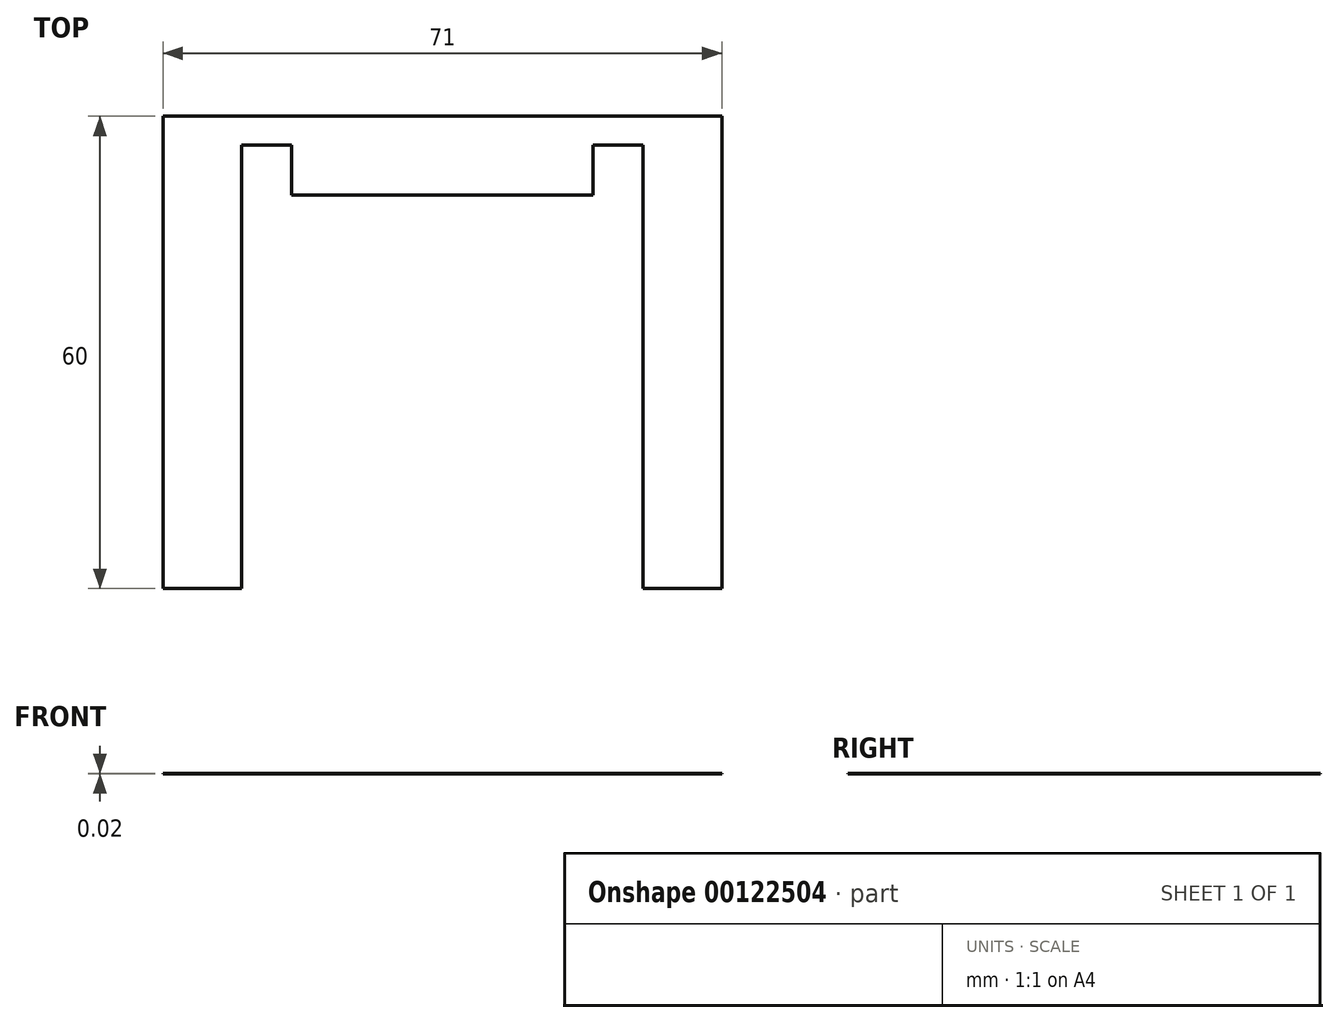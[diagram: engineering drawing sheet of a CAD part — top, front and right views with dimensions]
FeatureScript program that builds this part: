
annotation { "Feature Type Name" : "Feature", "Feature Type Description" : "" }
export const myFeature = defineFeature(function(context is Context, id is Id, definition is map)
    precondition{}
    {
        {
            var Q0;
            Q0=qCreatedBy(makeId("Top.planeOp"),FACE);
            var sketch = newSketch(context, id + "F0", { "sketchPlane" : qUnion([Q0])});
            skLineSegment(sketch, "E0.bottom", {"start": v(0, 0) * mm, "end": v(71, 0) * mm});
            skLineSegment(sketch, "E0.top", {"start": v(0, 60) * mm, "end": v(71, 60) * mm});
            skLineSegment(sketch, "E0.left", {"start": v(0, 0) * mm, "end": v(0, 60) * mm});
            skLineSegment(sketch, "E0.right", {"start": v(71, 0) * mm, "end": v(71, 60) * mm});
            skLineSegment(sketch, "E1", {"start": v(35.5, 60) * mm, "end": v(35.5, 0) * mm, "construction": true});
            skLineSegment(sketch, "E2", {"start": v(19.5, 43) * mm, "end": v(51.5, 43) * mm, "construction": true});
            skPoint(sketch, "E3", {"position": v(35.5, 43) * mm});
            skPoint(sketch, "E4", {"position": v(35.5, 50) * mm});
            skLineSegment(sketch, "E5", {"start": v(10, 50) * mm, "end": v(10, 0) * mm});
            skLineSegment(sketch, "E6", {"start": v(61, 50) * mm, "end": v(61, 0) * mm});
            skCircle(sketch, "E7", {"center": v(19.5, 43) * mm, "radius": 2.5 * mm});
            skCircle(sketch, "E8", {"center": v(51.5, 43) * mm, "radius": 2.5 * mm});
            skLineSegment(sketch, "E9", {"start": v(10, 50) * mm, "end": v(10, 56.35) * mm});
            skLineSegment(sketch, "E10", {"start": v(10, 56.35) * mm, "end": v(16.35, 56.35) * mm});
            skLineSegment(sketch, "E11", {"start": v(16.35, 56.35) * mm, "end": v(16.35, 50) * mm});
            skLineSegment(sketch, "E12.MirrorCS", {"start": v(54.65, 56.35) * mm, "end": v(54.65, 50) * mm});
            skLineSegment(sketch, "E13.MirrorCS", {"start": v(54.65, 50) * mm, "end": v(16.35, 50) * mm});
            skLineSegment(sketch, "E14.MirrorCS", {"start": v(61, 50) * mm, "end": v(61, 56.35) * mm});
            skLineSegment(sketch, "E15.MirrorCS", {"start": v(61, 56.35) * mm, "end": v(54.65, 56.35) * mm});
            skLineSegment(sketch, "E16", {"start": v(16.35, 50) * mm, "end": v(10, 50) * mm, "construction": true});
            skLineSegment(sketch, "E17", {"start": v(61, 50) * mm, "end": v(54.65, 50) * mm, "construction": true});
            skLineSegment(sketch, "E18", {"start": v(16.35, 56.35) * mm, "end": v(54.65, 56.35) * mm, "construction": true});
            skSolve(sketch);
        }
        {
            var Q0;
            {var subQ5=sQuery(id+"F0.wireOp",EDGE,"E0.left");Q0=makeQuery(id+"F0.imprint","IMPRINT",FACE,{"disambiguationData":[TD([[makeQuery(id+"F0.imprint","IMPRINT",EDGE,{"derivedFrom":subQ5}),-1.0]])]});}
            var Q1;
            {var subQ0=sQuery(id+"F0.wireOp",EDGE,"E5");Q1=makeQuery(id+"F0.imprint","IMPRINT",FACE,{"disambiguationData":[TD([[makeQuery(id+"F0.imprint","IMPRINT",EDGE,{"derivedFrom":subQ0}),1.0]])]});}
            var Q2;
            {var subQ0=sQuery(id+"F0.wireOp",EDGE,"E6");Q2=makeQuery(id+"F0.imprint","IMPRINT",FACE,{"disambiguationData":[TD([[makeQuery(id+"F0.imprint","IMPRINT",EDGE,{"derivedFrom":subQ0}),-1.0]])]});}
            var Q3;
            {var subQ5=sQuery(id+"F0.wireOp",EDGE,"E0.right");Q3=makeQuery(id+"F0.imprint","IMPRINT",FACE,{"disambiguationData":[TD([[makeQuery(id+"F0.imprint","IMPRINT",EDGE,{"derivedFrom":subQ5}),1.0]])]});}
            extrude(context, id + "F1", {"entities" : qUnion([Q0, Q1, Q2, Q3]), "oppositeDirection" : true, "depth" : 1 / 50.8 * mm});
        }
        {
            var Q0;
            Q0=makeQuery(id+"F0.imprint","IMPRINT",FACE,{"disambiguationData":[TD([[makeQuery(id+"F0.imprint","IMPRINT",EDGE,{"derivedFrom":sQuery(id+"F0.wireOp",EDGE,"gX3SNZyY-rRDi-3Qxw-gn3m-8xi9fO2PBAxc")}),-1.0]])]});
            var Q1;
            {var subQ0=sQuery(id+"F0.wireOp",EDGE,"E5");Q1=makeQuery(id+"F0.imprint","IMPRINT",FACE,{"disambiguationData":[TD([[makeQuery(id+"F0.imprint","IMPRINT",EDGE,{"derivedFrom":subQ0}),1.0]])]});}
            extrude(context, id + "F2", {"entities" : qUnion([Q0, Q1]), "operationType" : NewBodyOperationType.REMOVE, "oppositeDirection" : true, "depth" : 4 * mm});
        }
    });
